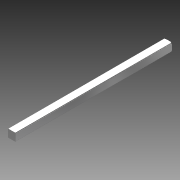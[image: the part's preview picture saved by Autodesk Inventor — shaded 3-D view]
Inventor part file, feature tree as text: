
AUTODESK INVENTOR PART (.ipt)
format: ipt  version: 2012 (Build 160160000, 160)  size: 119,296 bytes
history: native  units: in
note: dims shown in document units (in); Inventor stores cm internally (conversion verified against a paired STEP export)
features: other x1, imported_body x1, plane x1, split x1
ambient origin geometry x8: Origin, YZ Plane, XZ Plane, XY Plane, X Axis, Y Axis, Z Axis, Center Point
feature tree (4):
  parser-record x1  (decoder bookkeeping rows leaked as tree rows — omitted from the tree; the rows remain in map.json)
  imported_body  "Base1"
  plane  "Work Plane1"
  split  "Split1"
